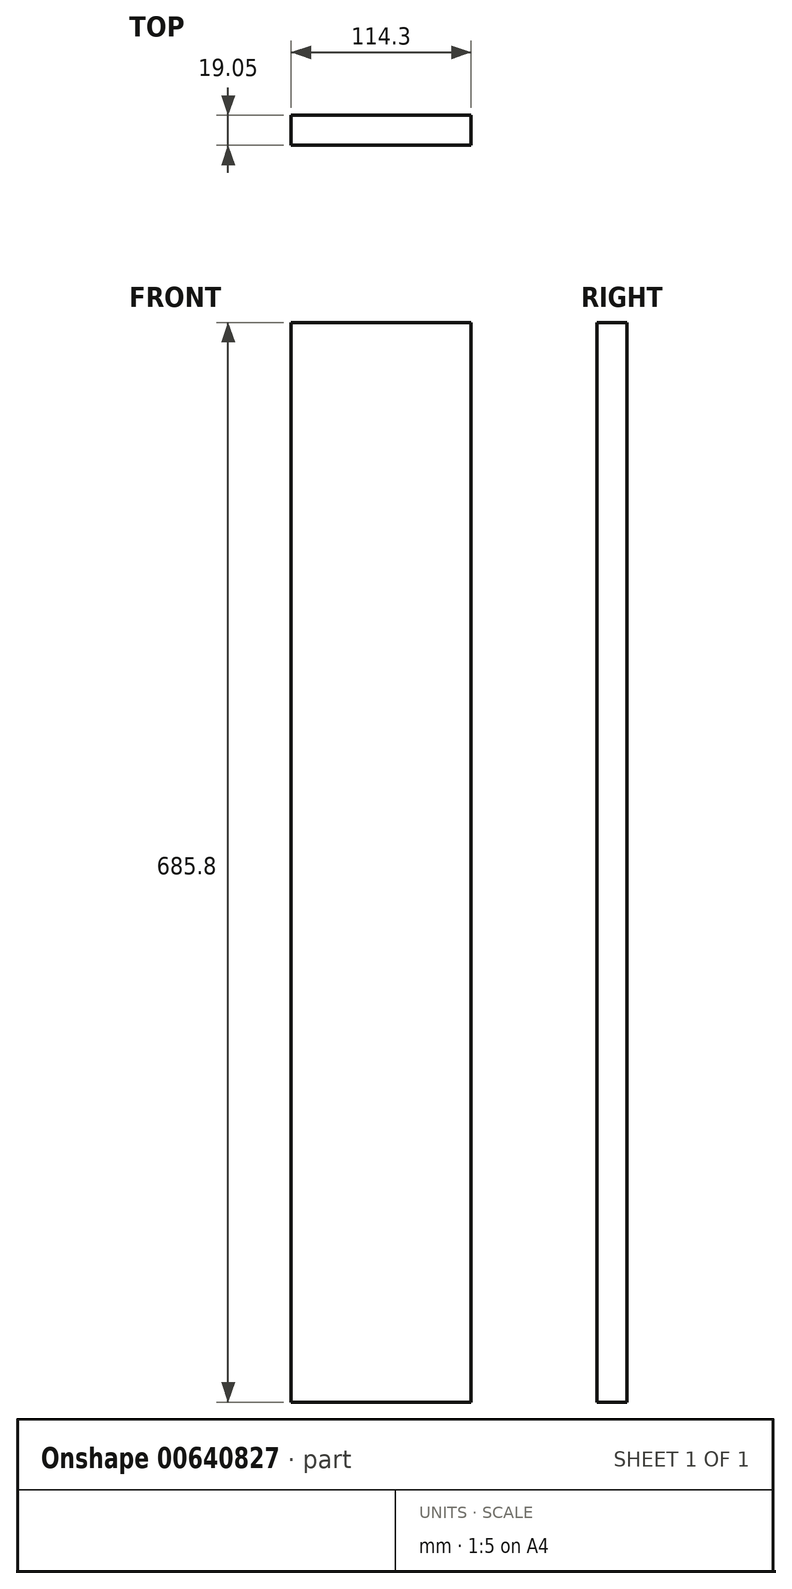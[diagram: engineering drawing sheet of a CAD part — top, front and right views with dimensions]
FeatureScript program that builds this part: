
annotation { "Feature Type Name" : "Feature", "Feature Type Description" : "" }
export const myFeature = defineFeature(function(context is Context, id is Id, definition is map)
    precondition{}
    {
        {
            var Q0;
            Q0=qCreatedBy(makeId("Front.planeOp"),FACE);
            var sketch = newSketch(context, id + "F0", { "sketchPlane" : qUnion([Q0])});
            skLineSegment(sketch, "E0.bottom", {"start": v(57.15, 342.9) * mm, "end": v(-57.15, 342.9) * mm});
            skLineSegment(sketch, "E0.top", {"start": v(57.15, -342.9) * mm, "end": v(-57.15, -342.9) * mm});
            skLineSegment(sketch, "E0.left", {"start": v(57.15, 342.9) * mm, "end": v(57.15, -342.9) * mm});
            skLineSegment(sketch, "E0.right", {"start": v(-57.15, 342.9) * mm, "end": v(-57.15, -342.9) * mm});
            skPoint(sketch, "E0.middle", {"position": v(0, 0) * mm});
            skSolve(sketch);
        }
        {
            var Q0;
            Q0=makeQuery(id+"F0.imprint","IMPRINT",FACE,{"disambiguationData":[TD([[makeQuery(id+"F0.imprint","IMPRINT",EDGE,{"derivedFrom":sQuery(id+"F0.wireOp",EDGE,"E0.bottom")}),1.0]])]});
            extrude(context, id + "F1", {"entities" : qUnion([Q0]), "depth" : 19.05 * mm, "offsetDistance" : 25.4 * mm});
        }
    });
